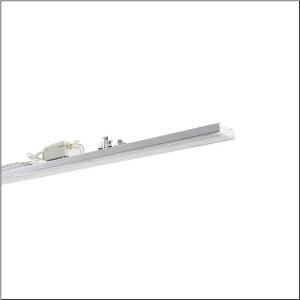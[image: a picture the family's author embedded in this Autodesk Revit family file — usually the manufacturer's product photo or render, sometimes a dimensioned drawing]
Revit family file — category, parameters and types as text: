
# Revit family: licross_21_recessed_mo_52tl12dn465g
name_source: partatom
category: Lighting Fixtures
units: mm (PartAtom-declared; Revit-internal decimal feet)

## family parameters
Cut with Voids When Loaded = No
Host = Face
Light Source = No
Part Type = Normal
Room Calculation Point = No
Round Connector Dimension = Use Diameter
Shared = No

## types (1)
- --- (1 x LED, 6500 lm, 35.1 W, 4000K)
    Apparent Load = 35 VA
    CIE Flux Codes = 72 92 99 100 100
    Color Rendering = 80
    Color Temperature = 4000K
    Default Elevation = 1800 mm
    Description = Licross 21 Recessed MO, luminaire insert, of sheet steel, galvanised, coil coated, white, length: 1.500mm, width: 66mm, height: 67mm, LED rated luminous flux: 6.500lm, light colour: 840, SDCM (Standard Deviation of Colour Matching)MacAdam ≤ 3 SDCM (initial), control gear: DALI 2, with plug, 5-pole, with phase selection, mains connection: 220..240V, AC, 50/60Hz, rated input power: 35W, internal wiring halogen-free, primary optical cover: cover, of PMMA, light emission: direct distribution, primary light characteristic: symmetric, protection rating (complete): IP40, insulation class (complete): insulation class I (protective earthing), certification: CE, ENEC, VDE, UKCA, protection symbol: D if used in an environment without relevant dust loads with corresponding accessories, impact resistance: IK06, permissible ambient temperature for indoor applications: -25..+45°C, corresponds to IFS (International Featured Standards) requirements for safety and quality in the food industry, reducing of maximum allowable ambient temperature of 5°C with ceiling mounting, LABS conformity tested according to VDMA 24364:2018-05, The light source and the operating device comply with the requirements of the Ecodesign Regulation (EU) 2019/2020 and are replaceable in accordance with this regulation, packaging unit: 1 piece
    Height = 58 mm
    Lamp = 1 x LED
    Lamp Light Flux = 6500 lm
    Lamp Power = 35.1 W
    Lamp count = 1
    Length = 1500 mm
    Luminous efficacy = 185 lm/W
    Manufacturer = Siteco
    ModVariant = No
    Model = 52TL12DN465G
    Mounting Place = Ceiling
    Mounting Type = Pendant
    Number of Poles = 1
    OnlyDefault = Yes
    Power Factor = 1
    Product Name = Licross 21 Recessed MO
    Product group = luminaire insert | ceiling pendant
    ProductGroupID = 901
    Protection Class = Protection class I
    Protection Degree = IP 40
    RLX_Detail_Level = 1
    RLX_Emergency_Light_Flux = 0 lm
    RLX_Emergency_Type = 0
    RLX_Emergency_Type_DB = No
    RlxData = <blob elided: 24561 chars, md5=4013a722>
    Socket = socket
    Standby Power = 0 W
    System Light Flux = 6500 lm
    System Power = 35 W
    Type Comments = factory setting: luminous flux: 100 % | dim-lin: 254 | 238 mA
    Type Image = l_1296930.jpg
    URL = http://relux.com
    VarID = @adj_127939
    Voltage = 0 V
    Weight = 0.00 kg
    Width = 66 mm

## geometry (parser evidence)
native form markers: Blend x4, Sweep x11
no freeform markers — native parametric forms only
